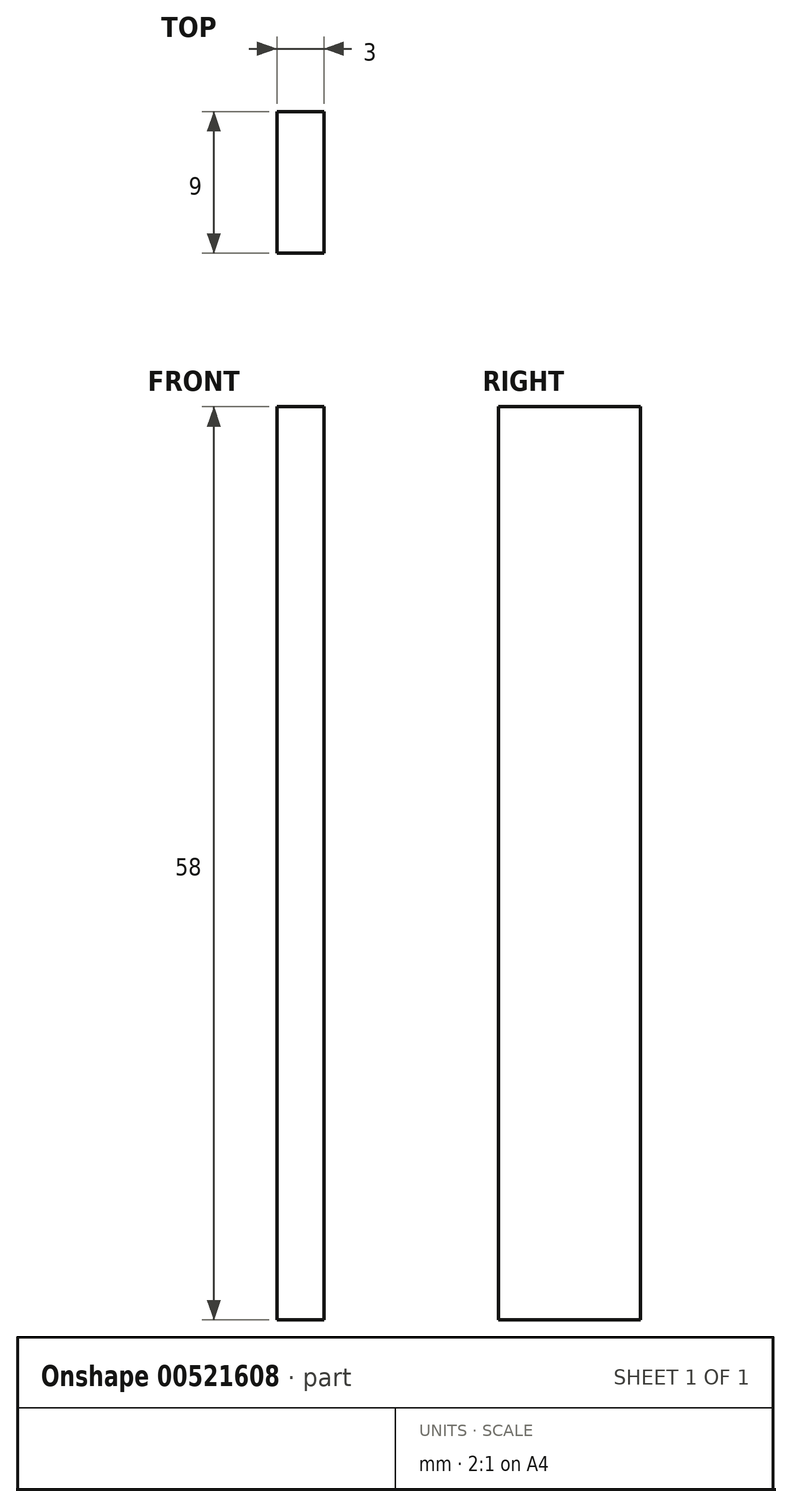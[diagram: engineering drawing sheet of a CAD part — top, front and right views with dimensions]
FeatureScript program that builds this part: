
annotation { "Feature Type Name" : "Feature", "Feature Type Description" : "" }
export const myFeature = defineFeature(function(context is Context, id is Id, definition is map)
    precondition{}
    {
        {
            var Q0;
            Q0=qCreatedBy(makeId("Right.planeOp"),FACE);
            var sketch = newSketch(context, id + "F0", { "sketchPlane" : qUnion([Q0])});
            skLineSegment(sketch, "E0.bottom", {"start": v(-4.5, 29) * mm, "end": v(4.5, 29) * mm});
            skLineSegment(sketch, "E0.top", {"start": v(-4.5, -29) * mm, "end": v(4.5, -29) * mm});
            skLineSegment(sketch, "E0.left", {"start": v(-4.5, 29) * mm, "end": v(-4.5, -29) * mm});
            skLineSegment(sketch, "E0.right", {"start": v(4.5, 29) * mm, "end": v(4.5, -29) * mm});
            skPoint(sketch, "E0.middle", {"position": v(0, 0) * mm});
            skSolve(sketch);
        }
        {
            var Q0;
            Q0=makeQuery(id+"F0.imprint","IMPRINT",FACE,{"disambiguationData":[TD([[makeQuery(id+"F0.imprint","IMPRINT",EDGE,{"derivedFrom":sQuery(id+"F0.wireOp",EDGE,"E0.bottom")}),-1.0]])]});
            extrude(context, id + "F1", {"entities" : qUnion([Q0]), "endBound" : BoundingType.SYMMETRIC, "depth" : 3 * mm, "offsetDistance" : 25 * mm});
        }
    });
